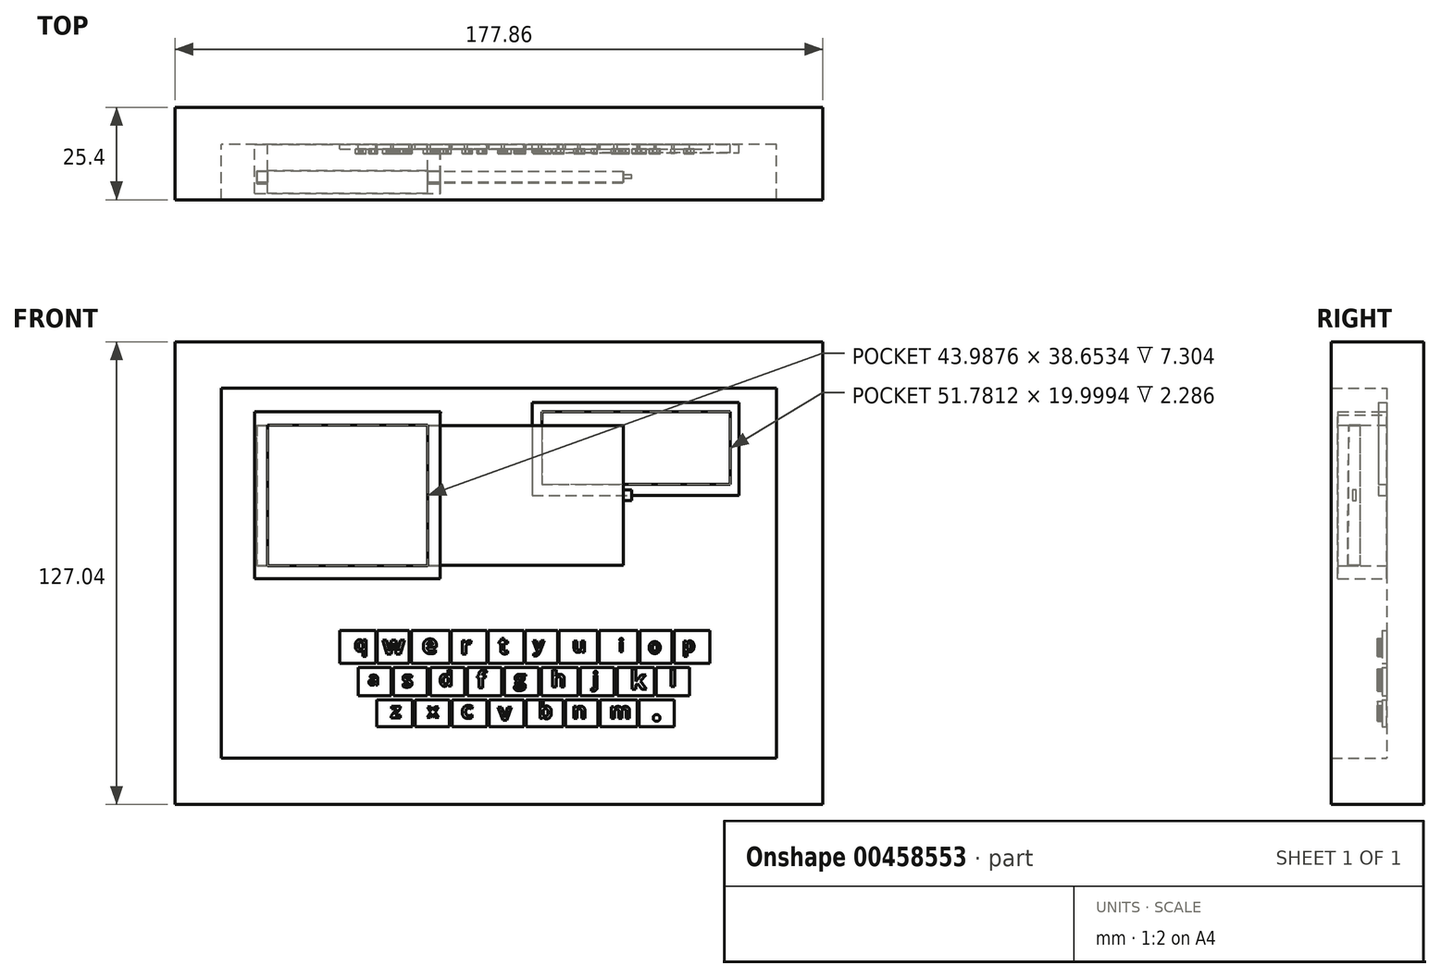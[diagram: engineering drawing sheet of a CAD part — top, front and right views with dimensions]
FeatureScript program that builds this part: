
annotation { "Feature Type Name" : "Feature", "Feature Type Description" : "" }
export const myFeature = defineFeature(function(context is Context, id is Id, definition is map)
    precondition{}
    {
        {
            var Q0;
            Q0=qCreatedBy(makeId("Front.planeOp"),FACE);
            var sketch = newSketch(context, id + "F0", { "sketchPlane" : qUnion([Q0])});
            skLineSegment(sketch, "E0", {"start": v(-71.85, 48.76) * mm, "end": v(-71.85, -52.84) * mm});
            skLineSegment(sketch, "E1", {"start": v(-71.85, -52.84) * mm, "end": v(80.55, -52.84) * mm});
            skLineSegment(sketch, "E2", {"start": v(80.55, -52.84) * mm, "end": v(80.55, 48.76) * mm});
            skLineSegment(sketch, "E3", {"start": v(80.55, 48.76) * mm, "end": v(-71.85, 48.76) * mm});
            skLineSegment(sketch, "E4", {"start": v(-84.56, 48.76) * mm, "end": v(-84.56, -52.84) * mm});
            skLineSegment(sketch, "E5", {"start": v(-84.56, 61.51) * mm, "end": v(93.3, 61.51) * mm});
            skLineSegment(sketch, "E6", {"start": v(93.24, -52.84) * mm, "end": v(93.3, 61.51) * mm});
            skLineSegment(sketch, "E7", {"start": v(-84.56, 61.51) * mm, "end": v(-84.56, 48.76) * mm});
            skLineSegment(sketch, "E8", {"start": v(-84.56, -52.84) * mm, "end": v(-84.56, -65.53) * mm});
            skLineSegment(sketch, "E9", {"start": v(-84.56, -65.53) * mm, "end": v(-71.85, -65.53) * mm});
            skLineSegment(sketch, "E10", {"start": v(93.3, -65.53) * mm, "end": v(-71.85, -65.53) * mm});
            skLineSegment(sketch, "E11", {"start": v(93.24, -52.84) * mm, "end": v(93.3, -65.53) * mm});
            skSolve(sketch);
        }
        {
            var Q0;
            Q0=makeQuery(id+"F0.imprint","IMPRINT",FACE,{"disambiguationData":[TD([[makeQuery(id+"F0.imprint","IMPRINT",EDGE,{"derivedFrom":sQuery(id+"F0.wireOp",EDGE,"E0")}),-1.0]])]});
            extrude(context, id + "F1", {"entities" : qUnion([Q0]), "depth" : 25.4 * mm});
        }
        {
            var Q0;
            Q0=makeQuery(id+"F0.imprint","IMPRINT",FACE,{"disambiguationData":[TD([[makeQuery(id+"F0.imprint","IMPRINT",EDGE,{"derivedFrom":sQuery(id+"F0.wireOp",EDGE,"E0")}),1.0]])]});
            extrude(context, id + "F2", {"entities" : qUnion([Q0]), "operationType" : NewBodyOperationType.ADD, "depth" : 10.16 * mm});
        }
        {
            var Q0;
            Q0=makeQuery(id+"F2.opExtrude","CAP_FACE",FACE,{"disambiguationData":[OSD([sQuery(id+"F0.wireOp",EDGE,"E0"),sQuery(id+"F0.wireOp",EDGE,"E1"),sQuery(id+"F0.wireOp",EDGE,"E2"),sQuery(id+"F0.wireOp",EDGE,"E3")])],"isStart":false});
            var sketch = newSketch(context, id + "F3", { "sketchPlane" : qUnion([Q0])});
            skLineSegment(sketch, "E12", {"start": v(-59.14, 38.65) * mm, "end": v(-59.14, 0) * mm});
            skLineSegment(sketch, "E13", {"start": v(-59.14, 0) * mm, "end": v(-15.15, 0) * mm});
            skLineSegment(sketch, "E14", {"start": v(-15.15, 0) * mm, "end": v(-15.15, 38.65) * mm});
            skLineSegment(sketch, "E15", {"start": v(-15.15, 38.65) * mm, "end": v(-59.14, 38.65) * mm});
            skLineSegment(sketch, "E16", {"start": v(-62.6, 41.32) * mm, "end": v(-62.6, -3.47) * mm});
            skLineSegment(sketch, "E17", {"start": v(-62.6, -3.47) * mm, "end": v(-11.69, -3.47) * mm});
            skLineSegment(sketch, "E18", {"start": v(-11.69, -3.47) * mm, "end": v(-11.69, 41.44) * mm});
            skLineSegment(sketch, "E19", {"start": v(-62.6, 42.34) * mm, "end": v(-11.64, 42.34) * mm});
            skLineSegment(sketch, "E20", {"start": v(-11.64, 42.34) * mm, "end": v(-11.69, 41.44) * mm});
            skLineSegment(sketch, "E21", {"start": v(-62.6, 41.32) * mm, "end": v(-62.6, 42.34) * mm});
            skLineSegment(sketch, "E22", {"start": v(16.14, 42.34) * mm, "end": v(16.14, 31.62) * mm});
            skLineSegment(sketch, "E23", {"start": v(16.14, 31.62) * mm, "end": v(16.14, 22.34) * mm});
            skLineSegment(sketch, "E24", {"start": v(16.14, 22.34) * mm, "end": v(67.93, 22.34) * mm});
            skLineSegment(sketch, "E25", {"start": v(67.93, 22.34) * mm, "end": v(67.93, 42.34) * mm});
            skLineSegment(sketch, "E26", {"start": v(67.93, 42.34) * mm, "end": v(16.14, 42.34) * mm});
            skLineSegment(sketch, "E27", {"start": v(13.54, 42.34) * mm, "end": v(13.54, 19.33) * mm});
            skLineSegment(sketch, "E28", {"start": v(13.54, 19.33) * mm, "end": v(70.28, 19.33) * mm});
            skLineSegment(sketch, "E29", {"start": v(70.28, 19.33) * mm, "end": v(70.28, 44.86) * mm});
            skLineSegment(sketch, "E30", {"start": v(70.28, 44.86) * mm, "end": v(13.54, 44.86) * mm});
            skLineSegment(sketch, "E31", {"start": v(13.54, 44.86) * mm, "end": v(13.54, 42.34) * mm});
            skLineSegment(sketch, "E32", {"start": v(-39.37, -17.81) * mm, "end": v(62.23, -17.81) * mm});
            skLineSegment(sketch, "E33", {"start": v(-39.37, -26.82) * mm, "end": v(62.23, -26.82) * mm});
            skLineSegment(sketch, "E34", {"start": v(-39.37, -26.82) * mm, "end": v(-29.2, -26.82) * mm});
            skLineSegment(sketch, "E35", {"start": v(-29.2, -26.82) * mm, "end": v(-19.94, -26.82) * mm});
            skLineSegment(sketch, "E36", {"start": v(-19.94, -26.82) * mm, "end": v(-8.88, -26.82) * mm});
            skLineSegment(sketch, "E37", {"start": v(-8.88, -26.82) * mm, "end": v(20.7, -26.82) * mm});
            skLineSegment(sketch, "E38", {"start": v(-8.88, -26.82) * mm, "end": v(11.43, -26.82) * mm});
            skLineSegment(sketch, "E39", {"start": v(20.7, -17.81) * mm, "end": v(42.81, -17.81) * mm});
            skLineSegment(sketch, "E40", {"start": v(42.81, -17.81) * mm, "end": v(62.23, -17.81) * mm});
            skLineSegment(sketch, "E41", {"start": v(52.52, -17.81) * mm, "end": v(52.52, -26.82) * mm});
            skLineSegment(sketch, "E42", {"start": v(-39.37, -17.81) * mm, "end": v(-39.37, -26.82) * mm});
            skLineSegment(sketch, "E43", {"start": v(-39.37, -26.82) * mm, "end": v(-34.29, -26.82) * mm});
            skLineSegment(sketch, "E44", {"start": v(-34.29, -26.82) * mm, "end": v(-34.29, -35.7) * mm});
            skLineSegment(sketch, "E45", {"start": v(62.23, -26.82) * mm, "end": v(56.7, -26.82) * mm});
            skLineSegment(sketch, "E46", {"start": v(56.7, -26.82) * mm, "end": v(56.7, -35.7) * mm});
            skLineSegment(sketch, "E47", {"start": v(-34.29, -26.82) * mm, "end": v(-24.57, -26.82) * mm});
            skLineSegment(sketch, "E48", {"start": v(-24.57, -26.82) * mm, "end": v(-24.57, -35.7) * mm});
            skLineSegment(sketch, "E49", {"start": v(-14.41, -26.82) * mm, "end": v(-14.41, -35.7) * mm});
            skLineSegment(sketch, "E50", {"start": v(-8.88, -26.82) * mm, "end": v(-4.25, -26.82) * mm});
            skLineSegment(sketch, "E51", {"start": v(-4.25, -26.82) * mm, "end": v(-4.25, -35.7) * mm});
            skLineSegment(sketch, "E52", {"start": v(-4.25, -26.82) * mm, "end": v(5.92, -26.82) * mm});
            skLineSegment(sketch, "E53", {"start": v(5.92, -26.82) * mm, "end": v(5.92, -35.7) * mm});
            skLineSegment(sketch, "E54", {"start": v(5.92, -26.82) * mm, "end": v(16.08, -26.82) * mm});
            skLineSegment(sketch, "E55", {"start": v(16.08, -26.82) * mm, "end": v(16.08, -35.7) * mm});
            skLineSegment(sketch, "E56", {"start": v(16.08, -26.82) * mm, "end": v(26.7, -26.82) * mm});
            skLineSegment(sketch, "E57", {"start": v(26.7, -26.82) * mm, "end": v(26.7, -35.7) * mm});
            skLineSegment(sketch, "E58", {"start": v(26.7, -26.82) * mm, "end": v(36.86, -26.82) * mm});
            skLineSegment(sketch, "E59", {"start": v(36.86, -26.82) * mm, "end": v(36.86, -35.7) * mm});
            skLineSegment(sketch, "E60", {"start": v(36.86, -26.82) * mm, "end": v(47.01, -26.82) * mm});
            skLineSegment(sketch, "E61", {"start": v(47.01, -26.82) * mm, "end": v(47.01, -35.7) * mm});
            skLineSegment(sketch, "E62", {"start": v(42.36, -35.7) * mm, "end": v(32.2, -35.7) * mm});
            skPoint(sketch, "E63.endSnap0", {"position": v(11.43, -35.7) * mm});
            skLineSegment(sketch, "E64", {"start": v(11.9, -35.7) * mm, "end": v(1.74, -35.7) * mm});
            skLineSegment(sketch, "E65", {"start": v(-8.42, -35.7) * mm, "end": v(-18.57, -35.7) * mm});
            skLineSegment(sketch, "E66", {"start": v(-39.37, -17.81) * mm, "end": v(-39.37, -26.69) * mm});
            skLineSegment(sketch, "E67", {"start": v(-29.2, -44.2) * mm, "end": v(-29.2, -35.7) * mm});
            skPoint(sketch, "E67.startSnap0", {"position": v(-29.2, -40.96) * mm});
            skLineSegment(sketch, "E68", {"start": v(-18.57, -35.7) * mm, "end": v(-18.57, -44.2) * mm});
            skLineSegment(sketch, "E69", {"start": v(-18.57, -44.2) * mm, "end": v(-8.42, -44.2) * mm});
            skLineSegment(sketch, "E70", {"start": v(-8.42, -44.2) * mm, "end": v(-8.42, -35.7) * mm});
            skLineSegment(sketch, "E71", {"start": v(1.74, -35.7) * mm, "end": v(1.74, -44.2) * mm});
            skPoint(sketch, "E71.endSnap0", {"position": v(1.74, -40.96) * mm});
            skLineSegment(sketch, "E72", {"start": v(1.74, -44.2) * mm, "end": v(11.9, -44.2) * mm});
            skLineSegment(sketch, "E73", {"start": v(11.9, -44.2) * mm, "end": v(11.9, -35.7) * mm});
            skLineSegment(sketch, "E74", {"start": v(22.05, -35.7) * mm, "end": v(22.05, -44.2) * mm});
            skLineSegment(sketch, "E75", {"start": v(22.05, -44.2) * mm, "end": v(32.2, -44.2) * mm});
            skLineSegment(sketch, "E76", {"start": v(32.2, -44.2) * mm, "end": v(32.2, -35.7) * mm});
            skLineSegment(sketch, "E77", {"start": v(42.36, -35.7) * mm, "end": v(42.36, -44.2) * mm});
            skLineSegment(sketch, "E78", {"start": v(42.36, -44.2) * mm, "end": v(52.52, -44.2) * mm});
            skLineSegment(sketch, "E79", {"start": v(52.52, -44.2) * mm, "end": v(52.52, -35.7) * mm});
            skLineSegment(sketch, "E80", {"start": v(62.23, -17.81) * mm, "end": v(62.23, -26.82) * mm});
            skLineSegment(sketch, "E81", {"start": v(-29.2, -44.2) * mm, "end": v(52.52, -44.2) * mm});
            skLineSegment(sketch, "E82", {"start": v(-34.29, -35.7) * mm, "end": v(56.7, -35.7) * mm});
            skText(sketch, "E83", { "text": "w", "fontName": "OpenSans-Bold.ttf"});
            skText(sketch, "E84", { "text": "e", "fontName": "OpenSans-Bold.ttf"});
            skText(sketch, "E85", { "text": "q", "fontName": "OpenSans-Bold.ttf"});
            skText(sketch, "E86", { "text": "r", "fontName": "OpenSans-Bold.ttf"});
            skText(sketch, "E87", { "text": "t", "fontName": "OpenSans-Bold.ttf"});
            skText(sketch, "E88", { "text": "y", "fontName": "OpenSans-Bold.ttf"});
            skText(sketch, "E89", { "text": "u", "fontName": "OpenSans-Bold.ttf"});
            skText(sketch, "E90", { "text": "i", "fontName": "OpenSans-Bold.ttf"});
            skText(sketch, "E91", { "text": "o", "fontName": "OpenSans-Bold.ttf"});
            skText(sketch, "E92", { "text": "p", "fontName": "OpenSans-Bold.ttf"});
            skText(sketch, "E93", { "text": "a", "fontName": "OpenSans-Bold.ttf"});
            skText(sketch, "E94", { "text": "s", "fontName": "OpenSans-Bold.ttf"});
            skText(sketch, "E95", { "text": "d", "fontName": "OpenSans-Bold.ttf"});
            skText(sketch, "E96", { "text": "f", "fontName": "OpenSans-Bold.ttf"});
            skText(sketch, "E97", { "text": "g", "fontName": "OpenSans-Bold.ttf"});
            skText(sketch, "E98", { "text": "h", "fontName": "OpenSans-Bold.ttf"});
            skText(sketch, "E99", { "text": "j", "fontName": "OpenSans-Bold.ttf"});
            skText(sketch, "E100", { "text": "k", "fontName": "OpenSans-Bold.ttf"});
            skText(sketch, "E101", { "text": "l", "fontName": "OpenSans-Bold.ttf"});
            skText(sketch, "E102", { "text": "z", "fontName": "OpenSans-Bold.ttf"});
            skText(sketch, "E103", { "text": "x", "fontName": "OpenSans-Bold.ttf"});
            skText(sketch, "E104", { "text": "c", "fontName": "OpenSans-Bold.ttf"});
            skText(sketch, "E105", { "text": "v", "fontName": "OpenSans-Bold.ttf"});
            skText(sketch, "E106", { "text": "b", "fontName": "OpenSans-Bold.ttf"});
            skText(sketch, "E107", { "text": "n", "fontName": "OpenSans-Bold.ttf"});
            skText(sketch, "E108", { "text": "m", "fontName": "OpenSans-Bold.ttf"});
            skText(sketch, "E109", { "text": ".", "fontName": "OpenSans-Bold.ttf"});
            skLineSegment(sketch, "E110", {"start": v(-29.45, -17.81) * mm, "end": v(-29.45, -26.82) * mm});
            skLineSegment(sketch, "E111", {"start": v(-28.96, -17.81) * mm, "end": v(-28.96, -26.82) * mm});
            skLineSegment(sketch, "E112", {"start": v(-20.19, -17.81) * mm, "end": v(-20.19, -26.82) * mm});
            skLineSegment(sketch, "E113", {"start": v(-19.66, -17.81) * mm, "end": v(-19.66, -26.82) * mm});
            skLineSegment(sketch, "E114", {"start": v(-9.13, -17.81) * mm, "end": v(-9.13, -26.82) * mm});
            skLineSegment(sketch, "E115", {"start": v(-8.63, -17.81) * mm, "end": v(-8.63, -26.82) * mm});
            skLineSegment(sketch, "E116", {"start": v(1.1, -17.81) * mm, "end": v(1.1, -26.82) * mm});
            skLineSegment(sketch, "E117", {"start": v(1.48, -17.81) * mm, "end": v(1.48, -26.82) * mm});
            skLineSegment(sketch, "E118", {"start": v(11.22, -17.79) * mm, "end": v(11.22, -26.82) * mm});
            skLineSegment(sketch, "E119", {"start": v(11.7, -17.81) * mm, "end": v(11.7, -26.82) * mm});
            skLineSegment(sketch, "E120", {"start": v(20.5, -17.81) * mm, "end": v(20.5, -26.82) * mm});
            skLineSegment(sketch, "E121", {"start": v(20.93, -17.81) * mm, "end": v(20.93, -26.82) * mm});
            skLineSegment(sketch, "E122", {"start": v(31.49, -17.81) * mm, "end": v(31.49, -26.82) * mm});
            skLineSegment(sketch, "E123", {"start": v(31.95, -17.81) * mm, "end": v(31.95, -26.82) * mm});
            skLineSegment(sketch, "E124", {"start": v(42.5, -17.81) * mm, "end": v(42.5, -26.82) * mm});
            skLineSegment(sketch, "E125", {"start": v(43.1, -17.81) * mm, "end": v(43.1, -26.82) * mm});
            skLineSegment(sketch, "E126", {"start": v(51.94, -17.81) * mm, "end": v(51.94, -26.82) * mm});
            skLineSegment(sketch, "E127", {"start": v(47.63, -26.82) * mm, "end": v(47.63, -35.7) * mm});
            skLineSegment(sketch, "E128", {"start": v(36, -26.82) * mm, "end": v(36, -35.7) * mm});
            skLineSegment(sketch, "E129", {"start": v(26.07, -26.82) * mm, "end": v(26.07, -35.7) * mm});
            skLineSegment(sketch, "E130", {"start": v(15.34, -26.82) * mm, "end": v(15.34, -35.7) * mm});
            skLineSegment(sketch, "E131", {"start": v(5.18, -26.82) * mm, "end": v(5.18, -35.7) * mm});
            skLineSegment(sketch, "E132", {"start": v(-5.02, -26.82) * mm, "end": v(-5.02, -35.7) * mm});
            skLineSegment(sketch, "E133", {"start": v(-15.24, -26.82) * mm, "end": v(-15.24, -35.7) * mm});
            skLineSegment(sketch, "E134", {"start": v(-25.25, -26.82) * mm, "end": v(-25.25, -35.7) * mm});
            skLineSegment(sketch, "E135", {"start": v(42.86, -35.7) * mm, "end": v(42.86, -44.2) * mm});
            skLineSegment(sketch, "E136", {"start": v(31.6, -35.7) * mm, "end": v(31.6, -44.2) * mm});
            skLineSegment(sketch, "E137", {"start": v(22.71, -35.7) * mm, "end": v(22.71, -44.2) * mm});
            skLineSegment(sketch, "E138", {"start": v(11.21, -35.7) * mm, "end": v(11.21, -44.2) * mm});
            skLineSegment(sketch, "E139", {"start": v(1.09, -35.7) * mm, "end": v(1.09, -44.2) * mm});
            skLineSegment(sketch, "E140", {"start": v(-9.15, -35.7) * mm, "end": v(-9.15, -44.2) * mm});
            skLineSegment(sketch, "E141", {"start": v(-19.37, -35.7) * mm, "end": v(-19.37, -44.2) * mm});
            skLineSegment(sketch, "E142", {"start": v(-29.2, -36.75) * mm, "end": v(52.52, -36.75) * mm});
            skLineSegment(sketch, "E143", {"start": v(-34.29, -27.87) * mm, "end": v(56.7, -27.87) * mm});
            const initialGuessF3  = {"E83": [-0.02753, -0.02422, 1, 0, 0.00506], "E84": [-0.0167, -0.02406, 1, 0, 0.00518], "E85": [-0.03527, -0.02345, 1, 0, 0.00409], "E86": [-0.00614, -0.02417, 1, 0, 0.00474], "E87": [0.00423, -0.02412, 1, 0, 0.00463], "E88": [0.01375, -0.02346, 1, 0, 0.0039], "E89": [0.0246, -0.02372, 1, 0, 0.00402], "E90": [0.03723, -0.02364, 1, 0, 0.00353], "E91": [0.04538, -0.02402, 1, 0, 0.00415], "E92": [0.05482, -0.02354, 1, 0, 0.00382], "E93": [-0.0315, -0.03273, 1, 0, 0.00355], "E94": [-0.02224, -0.03327, 1, 0, 0.00439], "E95": [-0.012, -0.03301, 1, 0, 0.00422], "E96": [-0.00171, -0.03352, 1, 0, 0.00458], "E97": [0.0086, -0.03291, 1, 0, 0.00406], "E98": [0.0187, -0.03322, 1, 0, 0.00448], "E99": [0.0301, -0.03306, 1, 0, 0.00392], "E100": [0.04034, -0.03392, 1, 0, 0.00529], "E101": [0.0512, -0.03308, 1, 0, 0.00444], "E102": [-0.0253, -0.0417, 1, 0, 0.0042], "E103": [-0.0153, -0.04163, 1, 0, 0.00391], "E104": [-0.00596, -0.04186, 1, 0, 0.0046], "E105": [0.0042, -0.04237, 1, 0, 0.0046], "E106": [0.01515, -0.04194, 1, 0, 0.00447], "E107": [0.02442, -0.04194, 1, 0, 0.00441], "E108": [0.03479, -0.04192, 1, 0, 0.0043], "E109": [0.04614, -0.04252, 1, 0, 0.0078]};
            skSetInitialGuess(sketch, initialGuessF3);
            skSolve(sketch);
        }
        {
            var Q0;
            Q0=makeQuery(id+"F3.imprint","IMPRINT",FACE,{"disambiguationData":[TD([[makeQuery(id+"F3.imprint","IMPRINT",EDGE,{"derivedFrom":sQuery(id+"F3.wireOp",EDGE,"E12")}),-1.0]])]});
            extrude(context, id + "F4", {"entities" : qUnion([Q0]), "operationType" : NewBodyOperationType.ADD, "depth" : 13.46 * mm});
        }
        {
            var Q0;
            Q0=makeQuery(id+"F3.imprint","IMPRINT",FACE,{"disambiguationData":[TD([[makeQuery(id+"F3.imprint","IMPRINT",EDGE,{"derivedFrom":sQuery(id+"F3.wireOp",EDGE,"E85.sketch_text.stroke-0")}),-1.0]])]});
            var Q1;
            Q1=makeQuery(id+"F3.imprint","IMPRINT",FACE,{"disambiguationData":[TD([[makeQuery(id+"F3.imprint","IMPRINT",EDGE,{"derivedFrom":sQuery(id+"F3.wireOp",EDGE,"E83.sketch_text.stroke-0")}),-1.0]])]});
            var Q2;
            Q2=makeQuery(id+"F3.imprint","IMPRINT",FACE,{"disambiguationData":[TD([[makeQuery(id+"F3.imprint","IMPRINT",EDGE,{"derivedFrom":sQuery(id+"F3.wireOp",EDGE,"E84.sketch_text.stroke-0")}),-1.0]])]});
            var Q3;
            Q3=makeQuery(id+"F3.imprint","IMPRINT",FACE,{"disambiguationData":[TD([[makeQuery(id+"F3.imprint","IMPRINT",EDGE,{"derivedFrom":sQuery(id+"F3.wireOp",EDGE,"E86.sketch_text.stroke-0")}),-1.0]])]});
            var Q4;
            Q4=makeQuery(id+"F3.imprint","IMPRINT",FACE,{"disambiguationData":[TD([[makeQuery(id+"F3.imprint","IMPRINT",EDGE,{"derivedFrom":sQuery(id+"F3.wireOp",EDGE,"E87.sketch_text.stroke-0")}),-1.0]])]});
            var Q5;
            Q5=makeQuery(id+"F3.imprint","IMPRINT",FACE,{"disambiguationData":[TD([[makeQuery(id+"F3.imprint","IMPRINT",EDGE,{"derivedFrom":sQuery(id+"F3.wireOp",EDGE,"E89.sketch_text.stroke-0")}),-1.0]])]});
            var Q6;
            Q6=makeQuery(id+"F3.imprint","IMPRINT",FACE,{"disambiguationData":[TD([[makeQuery(id+"F3.imprint","IMPRINT",EDGE,{"derivedFrom":sQuery(id+"F3.wireOp",EDGE,"E88.sketch_text.stroke-0")}),-1.0]])]});
            var Q7;
            Q7=makeQuery(id+"F3.imprint","IMPRINT",FACE,{"disambiguationData":[TD([[makeQuery(id+"F3.imprint","IMPRINT",EDGE,{"derivedFrom":sQuery(id+"F3.wireOp",EDGE,"E91.sketch_text.stroke-0")}),-1.0]])]});
            var Q8;
            Q8=makeQuery(id+"F3.imprint","IMPRINT",FACE,{"disambiguationData":[TD([[makeQuery(id+"F3.imprint","IMPRINT",EDGE,{"derivedFrom":sQuery(id+"F3.wireOp",EDGE,"E90.sketch_text.stroke-5")}),-1.0]])]});
            var Q9;
            Q9=makeQuery(id+"F3.imprint","IMPRINT",FACE,{"disambiguationData":[TD([[makeQuery(id+"F3.imprint","IMPRINT",EDGE,{"derivedFrom":sQuery(id+"F3.wireOp",EDGE,"E90.sketch_text.stroke-0")}),-1.0]])]});
            var Q10;
            Q10=makeQuery(id+"F3.imprint","IMPRINT",FACE,{"disambiguationData":[TD([[makeQuery(id+"F3.imprint","IMPRINT",EDGE,{"derivedFrom":sQuery(id+"F3.wireOp",EDGE,"E92.sketch_text.stroke-0")}),-1.0]])]});
            var Q11;
            Q11=makeQuery(id+"F3.imprint","IMPRINT",FACE,{"disambiguationData":[TD([[makeQuery(id+"F3.imprint","IMPRINT",EDGE,{"derivedFrom":sQuery(id+"F3.wireOp",EDGE,"E101.sketch_text.stroke-0")}),-1.0]])]});
            var Q12;
            Q12=makeQuery(id+"F3.imprint","IMPRINT",FACE,{"disambiguationData":[TD([[makeQuery(id+"F3.imprint","IMPRINT",EDGE,{"derivedFrom":sQuery(id+"F3.wireOp",EDGE,"E100.sketch_text.stroke-0")}),-1.0]])]});
            var Q13;
            Q13=makeQuery(id+"F3.imprint","IMPRINT",FACE,{"disambiguationData":[TD([[makeQuery(id+"F3.imprint","IMPRINT",EDGE,{"derivedFrom":sQuery(id+"F3.wireOp",EDGE,"E99.sketch_text.stroke-0")}),-1.0]])]});
            var Q14;
            Q14=makeQuery(id+"F3.imprint","IMPRINT",FACE,{"disambiguationData":[TD([[makeQuery(id+"F3.imprint","IMPRINT",EDGE,{"derivedFrom":sQuery(id+"F3.wireOp",EDGE,"E99.sketch_text.stroke-10")}),-1.0]])]});
            var Q15;
            Q15=makeQuery(id+"F3.imprint","IMPRINT",FACE,{"disambiguationData":[TD([[makeQuery(id+"F3.imprint","IMPRINT",EDGE,{"derivedFrom":sQuery(id+"F3.wireOp",EDGE,"E98.sketch_text.stroke-0")}),-1.0]])]});
            var Q16;
            Q16=makeQuery(id+"F3.imprint","IMPRINT",FACE,{"disambiguationData":[TD([[makeQuery(id+"F3.imprint","IMPRINT",EDGE,{"derivedFrom":sQuery(id+"F3.wireOp",EDGE,"E97.sketch_text.stroke-0")}),-1.0]])]});
            var Q17;
            Q17=makeQuery(id+"F3.imprint","IMPRINT",FACE,{"disambiguationData":[TD([[makeQuery(id+"F3.imprint","IMPRINT",EDGE,{"derivedFrom":sQuery(id+"F3.wireOp",EDGE,"E96.sketch_text.stroke-0")}),-1.0]])]});
            var Q18;
            Q18=makeQuery(id+"F3.imprint","IMPRINT",FACE,{"disambiguationData":[TD([[makeQuery(id+"F3.imprint","IMPRINT",EDGE,{"derivedFrom":sQuery(id+"F3.wireOp",EDGE,"E95.sketch_text.stroke-0")}),-1.0]])]});
            var Q19;
            Q19=makeQuery(id+"F3.imprint","IMPRINT",FACE,{"disambiguationData":[TD([[makeQuery(id+"F3.imprint","IMPRINT",EDGE,{"derivedFrom":sQuery(id+"F3.wireOp",EDGE,"E94.sketch_text.stroke-0")}),-1.0]])]});
            var Q20;
            Q20=makeQuery(id+"F3.imprint","IMPRINT",FACE,{"disambiguationData":[TD([[makeQuery(id+"F3.imprint","IMPRINT",EDGE,{"derivedFrom":sQuery(id+"F3.wireOp",EDGE,"E93.sketch_text.stroke-0")}),-1.0]])]});
            var Q21;
            Q21=makeQuery(id+"F3.imprint","IMPRINT",FACE,{"disambiguationData":[TD([[makeQuery(id+"F3.imprint","IMPRINT",EDGE,{"derivedFrom":sQuery(id+"F3.wireOp",EDGE,"E102.sketch_text.stroke-0")}),-1.0]])]});
            var Q22;
            Q22=makeQuery(id+"F3.imprint","IMPRINT",FACE,{"disambiguationData":[TD([[makeQuery(id+"F3.imprint","IMPRINT",EDGE,{"derivedFrom":sQuery(id+"F3.wireOp",EDGE,"E103.sketch_text.stroke-0")}),-1.0]])]});
            var Q23;
            Q23=makeQuery(id+"F3.imprint","IMPRINT",FACE,{"disambiguationData":[TD([[makeQuery(id+"F3.imprint","IMPRINT",EDGE,{"derivedFrom":sQuery(id+"F3.wireOp",EDGE,"E104.sketch_text.stroke-0")}),-1.0]])]});
            var Q24;
            Q24=makeQuery(id+"F3.imprint","IMPRINT",FACE,{"disambiguationData":[TD([[makeQuery(id+"F3.imprint","IMPRINT",EDGE,{"derivedFrom":sQuery(id+"F3.wireOp",EDGE,"E105.sketch_text.stroke-0")}),-1.0]])]});
            var Q25;
            Q25=makeQuery(id+"F3.imprint","IMPRINT",FACE,{"disambiguationData":[TD([[makeQuery(id+"F3.imprint","IMPRINT",EDGE,{"derivedFrom":sQuery(id+"F3.wireOp",EDGE,"E106.sketch_text.stroke-0")}),-1.0]])]});
            var Q26;
            Q26=makeQuery(id+"F3.imprint","IMPRINT",FACE,{"disambiguationData":[TD([[makeQuery(id+"F3.imprint","IMPRINT",EDGE,{"derivedFrom":sQuery(id+"F3.wireOp",EDGE,"E109.sketch_text.stroke-0")}),-1.0]])]});
            var Q27;
            Q27=makeQuery(id+"F3.imprint","IMPRINT",FACE,{"disambiguationData":[TD([[makeQuery(id+"F3.imprint","IMPRINT",EDGE,{"derivedFrom":sQuery(id+"F3.wireOp",EDGE,"E108.sketch_text.stroke-0")}),-1.0]])]});
            var Q28;
            Q28=makeQuery(id+"F3.imprint","IMPRINT",FACE,{"disambiguationData":[TD([[makeQuery(id+"F3.imprint","IMPRINT",EDGE,{"derivedFrom":sQuery(id+"F3.wireOp",EDGE,"E107.sketch_text.stroke-0")}),-1.0]])]});
            extrude(context, id + "F5", {"entities" : qUnion([Q0, Q1, Q2, Q3, Q4, Q5, Q6, Q7, Q8, Q9, Q10, Q11, Q12, Q13, Q14, Q15, Q16, Q17, Q18, Q19, Q20, Q21, Q22, Q23, Q24, Q25, Q26, Q27, Q28]), "operationType" : NewBodyOperationType.ADD, "depth" : 2.54 * mm});
        }
        {
            var Q0;
            Q0=makeQuery(id+"F3.imprint","IMPRINT",FACE,{"disambiguationData":[TD([[makeQuery(id+"F3.imprint","IMPRINT",EDGE,{"derivedFrom":sQuery(id+"F3.wireOp",EDGE,"E22")}),-1.0]])]});
            extrude(context, id + "F6", {"entities" : qUnion([Q0]), "operationType" : NewBodyOperationType.ADD, "depth" : 2.3 * mm});
        }
        {
            var Q0;
            Q0=makeQuery(id+"F3.imprint","IMPRINT",FACE,{"disambiguationData":[TD([[makeQuery(id+"F3.imprint","IMPRINT",EDGE,{"derivedFrom":sQuery(id+"F3.wireOp",EDGE,"E42")}),1.0]])]});
            var Q1;
            Q1=makeQuery(id+"F3.imprint","IMPRINT",FACE,{"disambiguationData":[TD([[makeQuery(id+"F3.imprint","IMPRINT",EDGE,{"derivedFrom":sQuery(id+"F3.wireOp",EDGE,"E83.sketch_text.stroke-0")}),1.0]])]});
            var Q2;
            Q2=makeQuery(id+"F3.imprint","IMPRINT",FACE,{"disambiguationData":[TD([[makeQuery(id+"F3.imprint","IMPRINT",EDGE,{"derivedFrom":sQuery(id+"F3.wireOp",EDGE,"E84.sketch_text.stroke-5")}),1.0]])]});
            var Q3;
            Q3=makeQuery(id+"F3.imprint","IMPRINT",FACE,{"disambiguationData":[TD([[makeQuery(id+"F3.imprint","IMPRINT",EDGE,{"derivedFrom":sQuery(id+"F3.wireOp",EDGE,"E86.sketch_text.stroke-0")}),1.0]])]});
            var Q4;
            Q4=makeQuery(id+"F3.imprint","IMPRINT",FACE,{"disambiguationData":[TD([[makeQuery(id+"F3.imprint","IMPRINT",EDGE,{"derivedFrom":sQuery(id+"F3.wireOp",EDGE,"E87.sketch_text.stroke-0")}),1.0]])]});
            var Q5;
            Q5=makeQuery(id+"F3.imprint","IMPRINT",FACE,{"disambiguationData":[TD([[makeQuery(id+"F3.imprint","IMPRINT",EDGE,{"derivedFrom":sQuery(id+"F3.wireOp",EDGE,"E88.sketch_text.stroke-0")}),1.0]])]});
            var Q6;
            Q6=makeQuery(id+"F3.imprint","IMPRINT",FACE,{"disambiguationData":[TD([[makeQuery(id+"F3.imprint","IMPRINT",EDGE,{"derivedFrom":sQuery(id+"F3.wireOp",EDGE,"E89.sketch_text.stroke-0")}),1.0]])]});
            var Q7;
            Q7=makeQuery(id+"F3.imprint","IMPRINT",FACE,{"disambiguationData":[TD([[makeQuery(id+"F3.imprint","IMPRINT",EDGE,{"derivedFrom":sQuery(id+"F3.wireOp",EDGE,"E90.sketch_text.stroke-0")}),1.0]])]});
            var Q8;
            Q8=makeQuery(id+"F3.imprint","IMPRINT",FACE,{"disambiguationData":[TD([[makeQuery(id+"F3.imprint","IMPRINT",EDGE,{"derivedFrom":sQuery(id+"F3.wireOp",EDGE,"E91.sketch_text.stroke-8")}),1.0]])]});
            var Q9;
            {var subQ2=sQuery(id+"F3.wireOp",EDGE,"E41");Q9=makeQuery(id+"F3.imprint","IMPRINT",FACE,{"disambiguationData":[TD([[makeQuery(id+"F3.imprint","IMPRINT",EDGE,{"derivedFrom":subQ2}),1.0]])]});}
            var Q10;
            Q10=makeQuery(id+"F3.imprint","IMPRINT",FACE,{"disambiguationData":[TD([[makeQuery(id+"F3.imprint","IMPRINT",EDGE,{"derivedFrom":sQuery(id+"F3.wireOp",EDGE,"E93.sketch_text.stroke-0")}),1.0]])]});
            var Q11;
            Q11=makeQuery(id+"F3.imprint","IMPRINT",FACE,{"disambiguationData":[TD([[makeQuery(id+"F3.imprint","IMPRINT",EDGE,{"derivedFrom":sQuery(id+"F3.wireOp",EDGE,"E94.sketch_text.stroke-0")}),1.0]])]});
            var Q12;
            Q12=makeQuery(id+"F3.imprint","IMPRINT",FACE,{"disambiguationData":[TD([[makeQuery(id+"F3.imprint","IMPRINT",EDGE,{"derivedFrom":sQuery(id+"F3.wireOp",EDGE,"E95.sketch_text.stroke-0")}),1.0]])]});
            var Q13;
            Q13=makeQuery(id+"F3.imprint","IMPRINT",FACE,{"disambiguationData":[TD([[makeQuery(id+"F3.imprint","IMPRINT",EDGE,{"derivedFrom":sQuery(id+"F3.wireOp",EDGE,"E96.sketch_text.stroke-0")}),1.0]])]});
            var Q14;
            Q14=makeQuery(id+"F3.imprint","IMPRINT",FACE,{"disambiguationData":[TD([[makeQuery(id+"F3.imprint","IMPRINT",EDGE,{"derivedFrom":sQuery(id+"F3.wireOp",EDGE,"E97.sketch_text.stroke-0")}),1.0]])]});
            var Q15;
            Q15=makeQuery(id+"F3.imprint","IMPRINT",FACE,{"disambiguationData":[TD([[makeQuery(id+"F3.imprint","IMPRINT",EDGE,{"derivedFrom":sQuery(id+"F3.wireOp",EDGE,"E98.sketch_text.stroke-0")}),1.0]])]});
            var Q16;
            Q16=makeQuery(id+"F3.imprint","IMPRINT",FACE,{"disambiguationData":[TD([[makeQuery(id+"F3.imprint","IMPRINT",EDGE,{"derivedFrom":sQuery(id+"F3.wireOp",EDGE,"E99.sketch_text.stroke-0")}),1.0]])]});
            var Q17;
            Q17=makeQuery(id+"F3.imprint","IMPRINT",FACE,{"disambiguationData":[TD([[makeQuery(id+"F3.imprint","IMPRINT",EDGE,{"derivedFrom":sQuery(id+"F3.wireOp",EDGE,"E100.sketch_text.stroke-0")}),1.0]])]});
            var Q18;
            Q18=makeQuery(id+"F3.imprint","IMPRINT",FACE,{"disambiguationData":[TD([[makeQuery(id+"F3.imprint","IMPRINT",EDGE,{"derivedFrom":sQuery(id+"F3.wireOp",EDGE,"E101.sketch_text.stroke-0")}),1.0]])]});
            var Q19;
            Q19=makeQuery(id+"F3.imprint","IMPRINT",FACE,{"disambiguationData":[TD([[makeQuery(id+"F3.imprint","IMPRINT",EDGE,{"derivedFrom":sQuery(id+"F3.wireOp",EDGE,"E109.sketch_text.stroke-0")}),1.0]])]});
            var Q20;
            Q20=makeQuery(id+"F3.imprint","IMPRINT",FACE,{"disambiguationData":[TD([[makeQuery(id+"F3.imprint","IMPRINT",EDGE,{"derivedFrom":sQuery(id+"F3.wireOp",EDGE,"E108.sketch_text.stroke-0")}),1.0]])]});
            var Q21;
            Q21=makeQuery(id+"F3.imprint","IMPRINT",FACE,{"disambiguationData":[TD([[makeQuery(id+"F3.imprint","IMPRINT",EDGE,{"derivedFrom":sQuery(id+"F3.wireOp",EDGE,"E107.sketch_text.stroke-0")}),1.0]])]});
            var Q22;
            Q22=makeQuery(id+"F3.imprint","IMPRINT",FACE,{"disambiguationData":[TD([[makeQuery(id+"F3.imprint","IMPRINT",EDGE,{"derivedFrom":sQuery(id+"F3.wireOp",EDGE,"E106.sketch_text.stroke-0")}),1.0]])]});
            var Q23;
            Q23=makeQuery(id+"F3.imprint","IMPRINT",FACE,{"disambiguationData":[TD([[makeQuery(id+"F3.imprint","IMPRINT",EDGE,{"derivedFrom":sQuery(id+"F3.wireOp",EDGE,"E105.sketch_text.stroke-0")}),1.0]])]});
            var Q24;
            Q24=makeQuery(id+"F3.imprint","IMPRINT",FACE,{"disambiguationData":[TD([[makeQuery(id+"F3.imprint","IMPRINT",EDGE,{"derivedFrom":sQuery(id+"F3.wireOp",EDGE,"E104.sketch_text.stroke-0")}),1.0]])]});
            var Q25;
            Q25=makeQuery(id+"F3.imprint","IMPRINT",FACE,{"disambiguationData":[TD([[makeQuery(id+"F3.imprint","IMPRINT",EDGE,{"derivedFrom":sQuery(id+"F3.wireOp",EDGE,"E103.sketch_text.stroke-0")}),1.0]])]});
            var Q26;
            Q26=makeQuery(id+"F3.imprint","IMPRINT",FACE,{"disambiguationData":[TD([[makeQuery(id+"F3.imprint","IMPRINT",EDGE,{"derivedFrom":sQuery(id+"F3.wireOp",EDGE,"E102.sketch_text.stroke-0")}),1.0]])]});
            var Q27;
            {var subQ0=sQuery(id+"F0.wireOp",EDGE,"E2");var subQ1=sQuery(id+"F0.wireOp",EDGE,"E1");var subQ2=sQuery(id+"F0.wireOp",EDGE,"E3");var subQ3=sQuery(id+"F0.wireOp",EDGE,"E0");Q27=makeQuery(id+"F5.boolean.opBoolean","SPLIT",FACE,{"disambiguationData":[TD([makeQuery(id+"F5.opExtrude","SWEPT_FACE",FACE,{"disambiguationData":[OSD([sQuery(id+"F3.wireOp",EDGE,"E85.sketch_text.stroke-0")])]})])],"derivedFrom":makeQuery(id+"F4.boolean.opBoolean","SPLIT",FACE,{"disambiguationData":[TD([makeQuery(id+"F1.opExtrude","SWEPT_FACE",FACE,{"disambiguationData":[OSD([subQ3])]})])],"derivedFrom":makeQuery(id+"F2.opExtrude","CAP_FACE",FACE,{"disambiguationData":[OSD([subQ3,subQ1,subQ0,subQ2])],"isStart":false})})});}
            var Q28;
            {var subQ0=sQuery(id+"F0.wireOp",EDGE,"E2");var subQ1=sQuery(id+"F0.wireOp",EDGE,"E1");var subQ2=sQuery(id+"F0.wireOp",EDGE,"E3");var subQ3=sQuery(id+"F0.wireOp",EDGE,"E0");Q28=makeQuery(id+"F5.boolean.opBoolean","SPLIT",FACE,{"disambiguationData":[TD([makeQuery(id+"F5.opExtrude","SWEPT_FACE",FACE,{"disambiguationData":[OSD([sQuery(id+"F3.wireOp",EDGE,"E84.sketch_text.stroke-0")])]})])],"derivedFrom":makeQuery(id+"F4.boolean.opBoolean","SPLIT",FACE,{"disambiguationData":[TD([makeQuery(id+"F1.opExtrude","SWEPT_FACE",FACE,{"disambiguationData":[OSD([subQ3])]})])],"derivedFrom":makeQuery(id+"F2.opExtrude","CAP_FACE",FACE,{"disambiguationData":[OSD([subQ3,subQ1,subQ0,subQ2])],"isStart":false})})});}
            var Q29;
            {var subQ0=sQuery(id+"F0.wireOp",EDGE,"E2");var subQ1=sQuery(id+"F0.wireOp",EDGE,"E1");var subQ2=sQuery(id+"F0.wireOp",EDGE,"E3");var subQ3=sQuery(id+"F0.wireOp",EDGE,"E0");Q29=makeQuery(id+"F5.boolean.opBoolean","SPLIT",FACE,{"disambiguationData":[TD([makeQuery(id+"F5.opExtrude","SWEPT_FACE",FACE,{"disambiguationData":[OSD([sQuery(id+"F3.wireOp",EDGE,"E95.sketch_text.stroke-14")])]})])],"derivedFrom":makeQuery(id+"F4.boolean.opBoolean","SPLIT",FACE,{"disambiguationData":[TD([makeQuery(id+"F1.opExtrude","SWEPT_FACE",FACE,{"disambiguationData":[OSD([subQ3])]})])],"derivedFrom":makeQuery(id+"F2.opExtrude","CAP_FACE",FACE,{"disambiguationData":[OSD([subQ3,subQ1,subQ0,subQ2])],"isStart":false})})});}
            var Q30;
            {var subQ0=sQuery(id+"F0.wireOp",EDGE,"E2");var subQ1=sQuery(id+"F0.wireOp",EDGE,"E1");var subQ2=sQuery(id+"F0.wireOp",EDGE,"E3");var subQ3=sQuery(id+"F0.wireOp",EDGE,"E0");Q30=makeQuery(id+"F5.boolean.opBoolean","SPLIT",FACE,{"disambiguationData":[TD([makeQuery(id+"F5.opExtrude","SWEPT_FACE",FACE,{"disambiguationData":[OSD([sQuery(id+"F3.wireOp",EDGE,"E93.sketch_text.stroke-18")])]})])],"derivedFrom":makeQuery(id+"F4.boolean.opBoolean","SPLIT",FACE,{"disambiguationData":[TD([makeQuery(id+"F1.opExtrude","SWEPT_FACE",FACE,{"disambiguationData":[OSD([subQ3])]})])],"derivedFrom":makeQuery(id+"F2.opExtrude","CAP_FACE",FACE,{"disambiguationData":[OSD([subQ3,subQ1,subQ0,subQ2])],"isStart":false})})});}
            var Q31;
            {var subQ0=sQuery(id+"F0.wireOp",EDGE,"E2");var subQ1=sQuery(id+"F0.wireOp",EDGE,"E1");var subQ2=sQuery(id+"F0.wireOp",EDGE,"E3");var subQ3=sQuery(id+"F0.wireOp",EDGE,"E0");Q31=makeQuery(id+"F5.boolean.opBoolean","SPLIT",FACE,{"disambiguationData":[TD([makeQuery(id+"F5.opExtrude","SWEPT_FACE",FACE,{"disambiguationData":[OSD([sQuery(id+"F3.wireOp",EDGE,"E97.sketch_text.stroke-29")])]})])],"derivedFrom":makeQuery(id+"F4.boolean.opBoolean","SPLIT",FACE,{"disambiguationData":[TD([makeQuery(id+"F1.opExtrude","SWEPT_FACE",FACE,{"disambiguationData":[OSD([subQ3])]})])],"derivedFrom":makeQuery(id+"F2.opExtrude","CAP_FACE",FACE,{"disambiguationData":[OSD([subQ3,subQ1,subQ0,subQ2])],"isStart":false})})});}
            var Q32;
            {var subQ0=sQuery(id+"F0.wireOp",EDGE,"E2");var subQ1=sQuery(id+"F0.wireOp",EDGE,"E1");var subQ2=sQuery(id+"F0.wireOp",EDGE,"E3");var subQ3=sQuery(id+"F0.wireOp",EDGE,"E0");Q32=makeQuery(id+"F5.boolean.opBoolean","SPLIT",FACE,{"disambiguationData":[TD([makeQuery(id+"F5.opExtrude","SWEPT_FACE",FACE,{"disambiguationData":[OSD([sQuery(id+"F3.wireOp",EDGE,"E97.sketch_text.stroke-38")])]})])],"derivedFrom":makeQuery(id+"F4.boolean.opBoolean","SPLIT",FACE,{"disambiguationData":[TD([makeQuery(id+"F1.opExtrude","SWEPT_FACE",FACE,{"disambiguationData":[OSD([subQ3])]})])],"derivedFrom":makeQuery(id+"F2.opExtrude","CAP_FACE",FACE,{"disambiguationData":[OSD([subQ3,subQ1,subQ0,subQ2])],"isStart":false})})});}
            var Q33;
            {var subQ0=sQuery(id+"F0.wireOp",EDGE,"E2");var subQ1=sQuery(id+"F0.wireOp",EDGE,"E1");var subQ2=sQuery(id+"F0.wireOp",EDGE,"E3");var subQ3=sQuery(id+"F0.wireOp",EDGE,"E0");Q33=makeQuery(id+"F5.boolean.opBoolean","SPLIT",FACE,{"disambiguationData":[TD([makeQuery(id+"F5.opExtrude","SWEPT_FACE",FACE,{"disambiguationData":[OSD([sQuery(id+"F3.wireOp",EDGE,"E106.sketch_text.stroke-14")])]})])],"derivedFrom":makeQuery(id+"F4.boolean.opBoolean","SPLIT",FACE,{"disambiguationData":[TD([makeQuery(id+"F1.opExtrude","SWEPT_FACE",FACE,{"disambiguationData":[OSD([subQ3])]})])],"derivedFrom":makeQuery(id+"F2.opExtrude","CAP_FACE",FACE,{"disambiguationData":[OSD([subQ3,subQ1,subQ0,subQ2])],"isStart":false})})});}
            var Q34;
            {var subQ0=sQuery(id+"F0.wireOp",EDGE,"E2");var subQ1=sQuery(id+"F0.wireOp",EDGE,"E1");var subQ2=sQuery(id+"F0.wireOp",EDGE,"E3");var subQ3=sQuery(id+"F0.wireOp",EDGE,"E0");Q34=makeQuery(id+"F5.boolean.opBoolean","SPLIT",FACE,{"disambiguationData":[TD([makeQuery(id+"F5.opExtrude","SWEPT_FACE",FACE,{"disambiguationData":[OSD([sQuery(id+"F3.wireOp",EDGE,"E92.sketch_text.stroke-15")])]})])],"derivedFrom":makeQuery(id+"F4.boolean.opBoolean","SPLIT",FACE,{"disambiguationData":[TD([makeQuery(id+"F1.opExtrude","SWEPT_FACE",FACE,{"disambiguationData":[OSD([subQ3])]})])],"derivedFrom":makeQuery(id+"F2.opExtrude","CAP_FACE",FACE,{"disambiguationData":[OSD([subQ3,subQ1,subQ0,subQ2])],"isStart":false})})});}
            var Q35;
            {var subQ0=sQuery(id+"F0.wireOp",EDGE,"E2");var subQ1=sQuery(id+"F0.wireOp",EDGE,"E1");var subQ2=sQuery(id+"F0.wireOp",EDGE,"E3");var subQ3=sQuery(id+"F0.wireOp",EDGE,"E0");Q35=makeQuery(id+"F5.boolean.opBoolean","SPLIT",FACE,{"disambiguationData":[TD([makeQuery(id+"F5.opExtrude","SWEPT_FACE",FACE,{"disambiguationData":[OSD([sQuery(id+"F3.wireOp",EDGE,"E91.sketch_text.stroke-0")])]})])],"derivedFrom":makeQuery(id+"F4.boolean.opBoolean","SPLIT",FACE,{"disambiguationData":[TD([makeQuery(id+"F1.opExtrude","SWEPT_FACE",FACE,{"disambiguationData":[OSD([subQ3])]})])],"derivedFrom":makeQuery(id+"F2.opExtrude","CAP_FACE",FACE,{"disambiguationData":[OSD([subQ3,subQ1,subQ0,subQ2])],"isStart":false})})});}
            extrude(context, id + "F7", {"entities" : qUnion([Q0, Q1, Q2, Q3, Q4, Q5, Q6, Q7, Q8, Q9, Q10, Q11, Q12, Q13, Q14, Q15, Q16, Q17, Q18, Q19, Q20, Q21, Q22, Q23, Q24, Q25, Q26, Q27, Q28, Q29, Q30, Q31, Q32, Q33, Q34, Q35]), "operationType" : NewBodyOperationType.ADD, "depth" : 1.27 * mm});
        }
        {
            var Q0;
            Q0=makeQuery(id+"F4.opExtrude","SWEPT_FACE",FACE,{"disambiguationData":[OSD([sQuery(id+"F3.wireOp",EDGE,"E18")])]});
            var sketch = newSketch(context, id + "F8", { "sketchPlane" : qUnion([Q0])});
            skLineSegment(sketch, "E144", {"start": v(-20.92, 0) * mm, "end": v(-20.6, 38.42) * mm});
            skLineSegment(sketch, "E145", {"start": v(-20.6, 38.65) * mm, "end": v(-20.6, 38.42) * mm});
            skLineSegment(sketch, "E146", {"start": v(-20.92, 0) * mm, "end": v(-17.46, -0.03) * mm});
            skLineSegment(sketch, "E147", {"start": v(-17.46, -0.03) * mm, "end": v(-17.46, 38.65) * mm});
            skLineSegment(sketch, "E148", {"start": v(-17.46, 38.65) * mm, "end": v(-20.6, 38.65) * mm});
            skLineSegment(sketch, "E149", {"start": v(-20.53, 38.54) * mm, "end": v(-17.57, 38.54) * mm});
            skPoint(sketch, "E149.startSnap0", {"position": v(-20.6, 38.54) * mm});
            skLineSegment(sketch, "E150", {"start": v(-17.57, 38.54) * mm, "end": v(-17.57, 0.17) * mm});
            skLineSegment(sketch, "E151", {"start": v(-17.57, 0.17) * mm, "end": v(-20.73, 0.2) * mm});
            skLineSegment(sketch, "E152", {"start": v(-20.73, 0.2) * mm, "end": v(-20.53, 38.54) * mm});
            skSolve(sketch);
        }
        {
            var Q0;
            Q0=makeQuery(id+"F8.imprint","IMPRINT",FACE,{"disambiguationData":[TD([[makeQuery(id+"F8.imprint","IMPRINT",EDGE,{"derivedFrom":sQuery(id+"F8.wireOp",EDGE,"E144")}),-1.0]])]});
            extrude(context, id + "F9", {"entities" : qUnion([Q0]), "operationType" : NewBodyOperationType.REMOVE, "oppositeDirection" : true, "depth" : 50.3 * mm});
        }
        {
            var Q0;
            Q0=makeQuery(id+"F9.boolean.opBoolean","SPLIT",FACE,{"disambiguationData":[TD([makeQuery(id+"F9.opExtrude","SWEPT_FACE",FACE,{"disambiguationData":[OSD([sQuery(id+"F8.wireOp",EDGE,"E149")])]})])],"derivedFrom":makeQuery(id+"F4.opExtrude","SWEPT_FACE",FACE,{"disambiguationData":[OSD([sQuery(id+"F3.wireOp",EDGE,"E18")])]})});
            extrude(context, id + "F10", {"entities" : qUnion([Q0]), "operationType" : NewBodyOperationType.ADD, "depth" : 50.3 * mm});
        }
        {
            var Q0;
            Q0=makeQuery(id+"F10.opExtrude","CAP_FACE",FACE,{"disambiguationData":[OSD([sQuery(id+"F3.wireOp",EDGE,"E18")])],"isStart":false});
            var sketch = newSketch(context, id + "F11", { "sketchPlane" : qUnion([Q0])});
            skLineSegment(sketch, "E153", {"start": v(-19.59, 17.91) * mm, "end": v(-18.56, 17.9) * mm});
            skLineSegment(sketch, "E154", {"start": v(-18.56, 17.9) * mm, "end": v(-18.56, 20.83) * mm});
            skLineSegment(sketch, "E155", {"start": v(-18.56, 20.83) * mm, "end": v(-19.59, 20.83) * mm});
            skLineSegment(sketch, "E156", {"start": v(-19.59, 20.83) * mm, "end": v(-19.59, 17.91) * mm});
            skSolve(sketch);
        }
        {
            var Q0;
            Q0=makeQuery(id+"F11.imprint","IMPRINT",FACE,{"disambiguationData":[TD([[makeQuery(id+"F11.imprint","IMPRINT",EDGE,{"derivedFrom":sQuery(id+"F11.wireOp",EDGE,"E153")}),1.0]])]});
            extrude(context, id + "F12", {"entities" : qUnion([Q0]), "operationType" : NewBodyOperationType.ADD, "depth" : 2.3 * mm});
        }
    });
